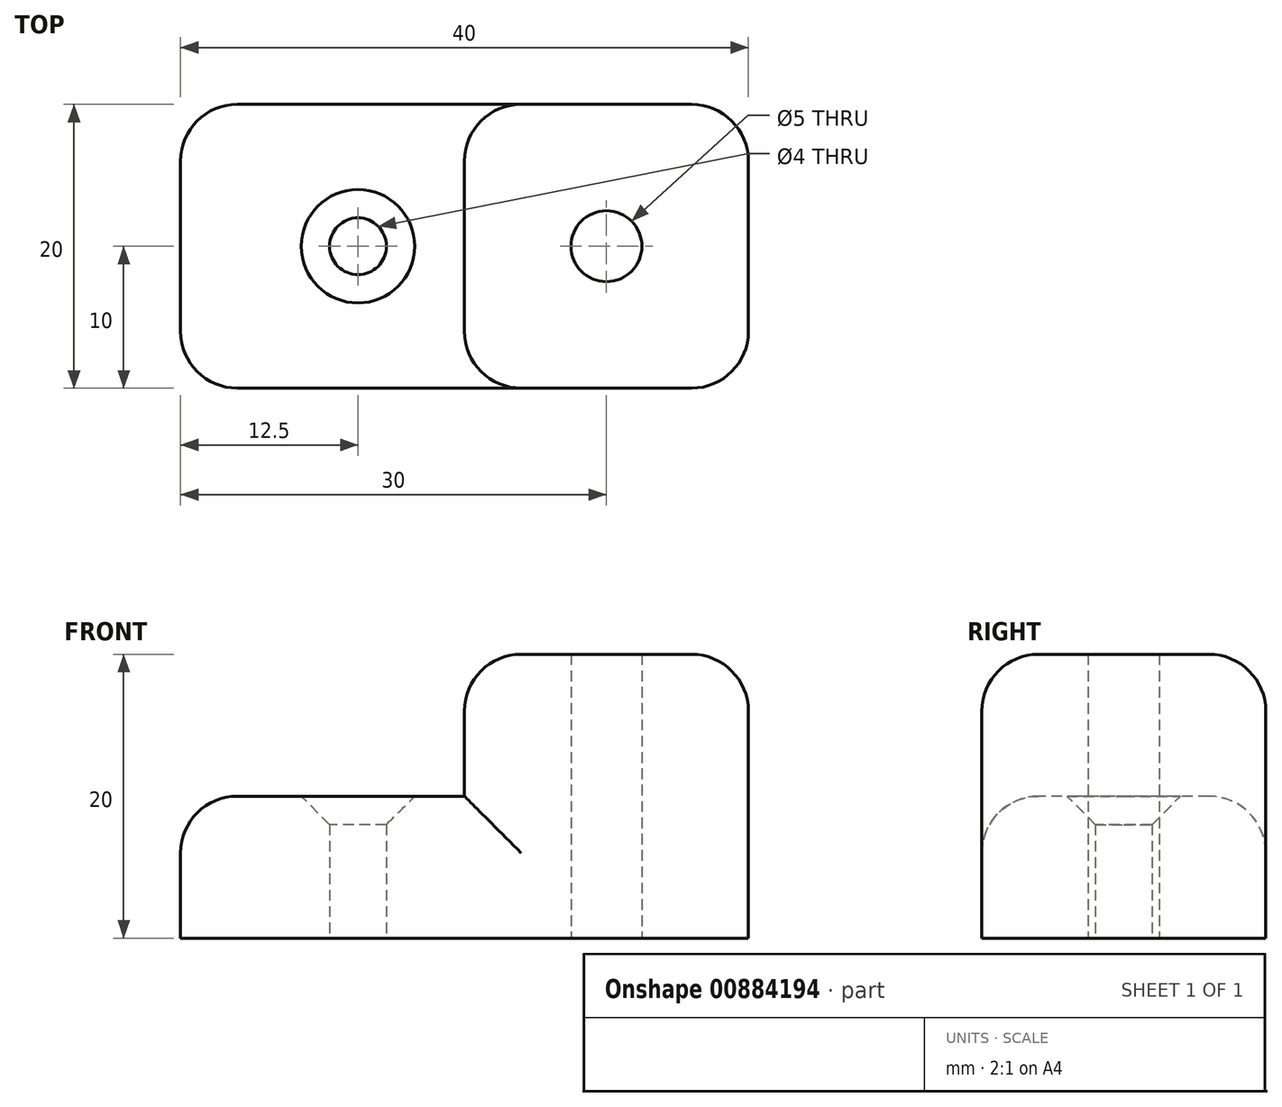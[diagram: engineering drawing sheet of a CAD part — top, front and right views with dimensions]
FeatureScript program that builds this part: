
annotation { "Feature Type Name" : "Feature", "Feature Type Description" : "" }
export const myFeature = defineFeature(function(context is Context, id is Id, definition is map)
    precondition{}
    {
        {
            var Q0;
            Q0=qCreatedBy(makeId("Top.planeOp"),FACE);
            var sketch = newSketch(context, id + "F0", { "sketchPlane" : qUnion([Q0])});
            skLineSegment(sketch, "E0.bottom", {"start": v(-30, 10) * mm, "end": v(10, 10) * mm});
            skLineSegment(sketch, "E0.top", {"start": v(-30, -10) * mm, "end": v(10, -10) * mm});
            skLineSegment(sketch, "E0.left", {"start": v(-30, 10) * mm, "end": v(-30, -10) * mm});
            skLineSegment(sketch, "E0.right", {"start": v(10, 10) * mm, "end": v(10, -10) * mm});
            skLineSegment(sketch, "E1", {"start": v(0, 0) * mm, "end": v(0, 10) * mm, "construction": true});
            skLineSegment(sketch, "E2", {"start": v(0, 0) * mm, "end": v(0, -10) * mm, "construction": true});
            skLineSegment(sketch, "E3", {"start": v(0, 0) * mm, "end": v(10, 0) * mm, "construction": true});
            skCircle(sketch, "E4", {"center": v(0, 0) * mm, "radius": 2.5 * mm});
            skLineSegment(sketch, "E5", {"start": v(-30, 0) * mm, "end": v(-17.5, 0) * mm});
            skCircle(sketch, "E6", {"center": v(-17.5, 0) * mm, "radius": 2 * mm});
            skSolve(sketch);
        }
        {
            var Q0;
            Q0=makeQuery(id+"F0.imprint","IMPRINT",FACE,{"disambiguationData":[TD([[makeQuery(id+"F0.imprint","IMPRINT",EDGE,{"derivedFrom":sQuery(id+"F0.wireOp",EDGE,"E0.bottom")}),-1.0]])]});
            extrude(context, id + "F1", {"entities" : qUnion([Q0]), "depth" : 10 * mm, "offsetDistance" : 25 * mm});
        }
        {
            var Q0;
            Q0=makeQuery(id+"F1.opExtrude","CAP_FACE",FACE,{"disambiguationData":[OSD([sQuery(id+"F0.wireOp",EDGE,"E0.bottom"),sQuery(id+"F0.wireOp",EDGE,"E0.top"),sQuery(id+"F0.wireOp",EDGE,"E0.left"),sQuery(id+"F0.wireOp",EDGE,"E0.right")])],"isStart":false});
            var sketch = newSketch(context, id + "F2", { "sketchPlane" : qUnion([Q0])});
            skLineSegment(sketch, "E7.bottom", {"start": v(10, 10) * mm, "end": v(-10, 10) * mm});
            skLineSegment(sketch, "E7.top", {"start": v(10, -10) * mm, "end": v(-10, -10) * mm});
            skLineSegment(sketch, "E7.left", {"start": v(10, 10) * mm, "end": v(10, -10) * mm});
            skLineSegment(sketch, "E7.right", {"start": v(-10, 10) * mm, "end": v(-10, -10) * mm});
            skSolve(sketch);
        }
        {
            var Q0;
            Q0=makeQuery(id+"F2.imprint","IMPRINT",FACE,{"disambiguationData":[TD([[makeQuery(id+"F2.imprint","IMPRINT",EDGE,{"derivedFrom":sQuery(id+"F2.wireOp",EDGE,"E7.bottom")}),-1.0]])]});
            extrude(context, id + "F3", {"entities" : qUnion([Q0]), "operationType" : NewBodyOperationType.ADD, "depth" : 10 * mm, "offsetDistance" : 25 * mm});
        }
        {
            var Q0;
            Q0=makeQuery(id+"F1.opExtrude","CAP_EDGE",EDGE,{"disambiguationData":[OSD([sQuery(id+"F0.wireOp",EDGE,"E0.left")])],"isStart":false});
            var Q1;
            Q1=makeQuery(id+"F1.opExtrude","CAP_EDGE",EDGE,{"disambiguationData":[OSD([sQuery(id+"F0.wireOp",EDGE,"E0.bottom")])],"isStart":false});
            var Q2;
            Q2=makeQuery(id+"F1.opExtrude","CAP_EDGE",EDGE,{"disambiguationData":[OSD([sQuery(id+"F0.wireOp",EDGE,"E0.top")])],"isStart":false});
            var Q3;
            Q3=makeQuery(id+"F3.opExtrude","CAP_EDGE",EDGE,{"disambiguationData":[OSD([sQuery(id+"F2.wireOp",EDGE,"E7.right")])],"isStart":false});
            var Q4;
            Q4=makeQuery(id+"F3.opExtrude","CAP_EDGE",EDGE,{"disambiguationData":[OSD([sQuery(id+"F2.wireOp",EDGE,"E7.bottom")])],"isStart":false});
            var Q5;
            Q5=makeQuery(id+"F3.opExtrude","CAP_EDGE",EDGE,{"disambiguationData":[OSD([sQuery(id+"F2.wireOp",EDGE,"E7.left")])],"isStart":false});
            var Q6;
            Q6=makeQuery(id+"F3.opExtrude","CAP_EDGE",EDGE,{"disambiguationData":[OSD([sQuery(id+"F2.wireOp",EDGE,"E7.top")])],"isStart":false});
            var Q7;
            Q7=makeQuery(id+"F3.opExtrude","SWEPT_EDGE",EDGE,{"disambiguationData":[OSD([sQuery(id+"F0.wireOp",EDGE,"E0.top"),sQuery(id+"F2.wireOp",EDGE,"E7.top"),sQuery(id+"F2.wireOp",EDGE,"E7.right")])]});
            var Q8;
            Q8=makeQuery(id+"F3.opExtrude","SWEPT_EDGE",EDGE,{"disambiguationData":[OSD([sQuery(id+"F0.wireOp",EDGE,"E0.bottom"),sQuery(id+"F2.wireOp",EDGE,"E7.bottom"),sQuery(id+"F2.wireOp",EDGE,"E7.right")])]});
            var Q9;
            Q9=makeQuery(id+"F3.boolean.opBoolean","MERGE",EDGE,{"derivedFrom":[makeQuery(id+"F1.opExtrude","SWEPT_EDGE",EDGE,{"disambiguationData":[OSD([sQuery(id+"F0.wireOp",EDGE,"E0.bottom"),sQuery(id+"F0.wireOp",EDGE,"E0.right")])]}),makeQuery(id+"F3.opExtrude","SWEPT_EDGE",EDGE,{"disambiguationData":[OSD([sQuery(id+"F2.wireOp",EDGE,"E7.bottom"),sQuery(id+"F2.wireOp",EDGE,"E7.left")])]})]});
            var Q10;
            Q10=makeQuery(id+"F3.boolean.opBoolean","MERGE",EDGE,{"derivedFrom":[makeQuery(id+"F1.opExtrude","SWEPT_EDGE",EDGE,{"disambiguationData":[OSD([sQuery(id+"F0.wireOp",EDGE,"E0.top"),sQuery(id+"F0.wireOp",EDGE,"E0.right")])]}),makeQuery(id+"F3.opExtrude","SWEPT_EDGE",EDGE,{"disambiguationData":[OSD([sQuery(id+"F2.wireOp",EDGE,"E7.top"),sQuery(id+"F2.wireOp",EDGE,"E7.left")])]})]});
            var Q11;
            Q11=makeQuery(id+"F1.opExtrude","SWEPT_EDGE",EDGE,{"disambiguationData":[OSD([sQuery(id+"F0.wireOp",EDGE,"E0.bottom"),sQuery(id+"F0.wireOp",EDGE,"E0.left")])]});
            var Q12;
            Q12=makeQuery(id+"F1.opExtrude","SWEPT_EDGE",EDGE,{"disambiguationData":[OSD([sQuery(id+"F0.wireOp",EDGE,"E0.top"),sQuery(id+"F0.wireOp",EDGE,"E0.left")])]});
            fillet(context, id + "F4", {"entities" : qUnion([Q0, Q1, Q2, Q3, Q4, Q5, Q6, Q7, Q8, Q9, Q10, Q11, Q12]), "radius" : 4 * mm, "tangentPropagation" : true, "allowEdgeOverflow" : false});
        }
        {
            var Q0;
            Q0=makeQuery(id+"F1.opExtrude","CAP_EDGE",EDGE,{"disambiguationData":[OSD([sQuery(id+"F0.wireOp",EDGE,"E6")])],"isStart":false});
            chamfer(context, id + "F5", {"entities" : qUnion([Q0]), "width" : 2 * mm, "tangentPropagation" : true});
        }
    });
